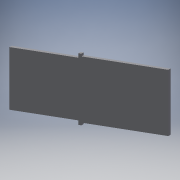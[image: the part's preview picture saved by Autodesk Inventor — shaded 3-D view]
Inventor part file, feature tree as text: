
AUTODESK INVENTOR PART (.ipt)
format: ipt  version: 2018.3 (Build 223284000, 284)  size: 1,031,168 bytes
history: native  units: mm
features: extrude x5, sketch x5
ambient origin geometry x8: Origin, YZ Plane, XZ Plane, XY Plane, X Axis, Y Axis, Z Axis, Center Point
bodies: Body1 (feature_tree)
feature tree (10):
  extrude  "Extrusion6"  Depth=150.0mm
  extrude  "Extrusion8"  Depth=3.0mm
  extrude  "Extrusion9"  Depth=3.0mm
  extrude  "Extrusion10"  Depth=2.0mm TaperAngle=0.0deg
  extrude  "Extrusion11"  Depth=3.0mm
  sketch  "Sketch6"  dims[d18=3.0mm d19=150.0mm]
  sketch  "Sketch8"  dims[d20=120.0deg d21=3.0mm]
  sketch  "Sketch9"  dims[d22=70.0mm d23=0.0mm d27=3.0mm]
  sketch  "Sketch10"  dims[d28=5.0mm d29=0.0mm d30=2.0mm d31=0.0mm]
  sketch  "Sketch11"  dims[d32=65.0mm d33=3.0mm d34=5.0mm d35=0.0mm d36=2.0mm d37=0.0mm]
